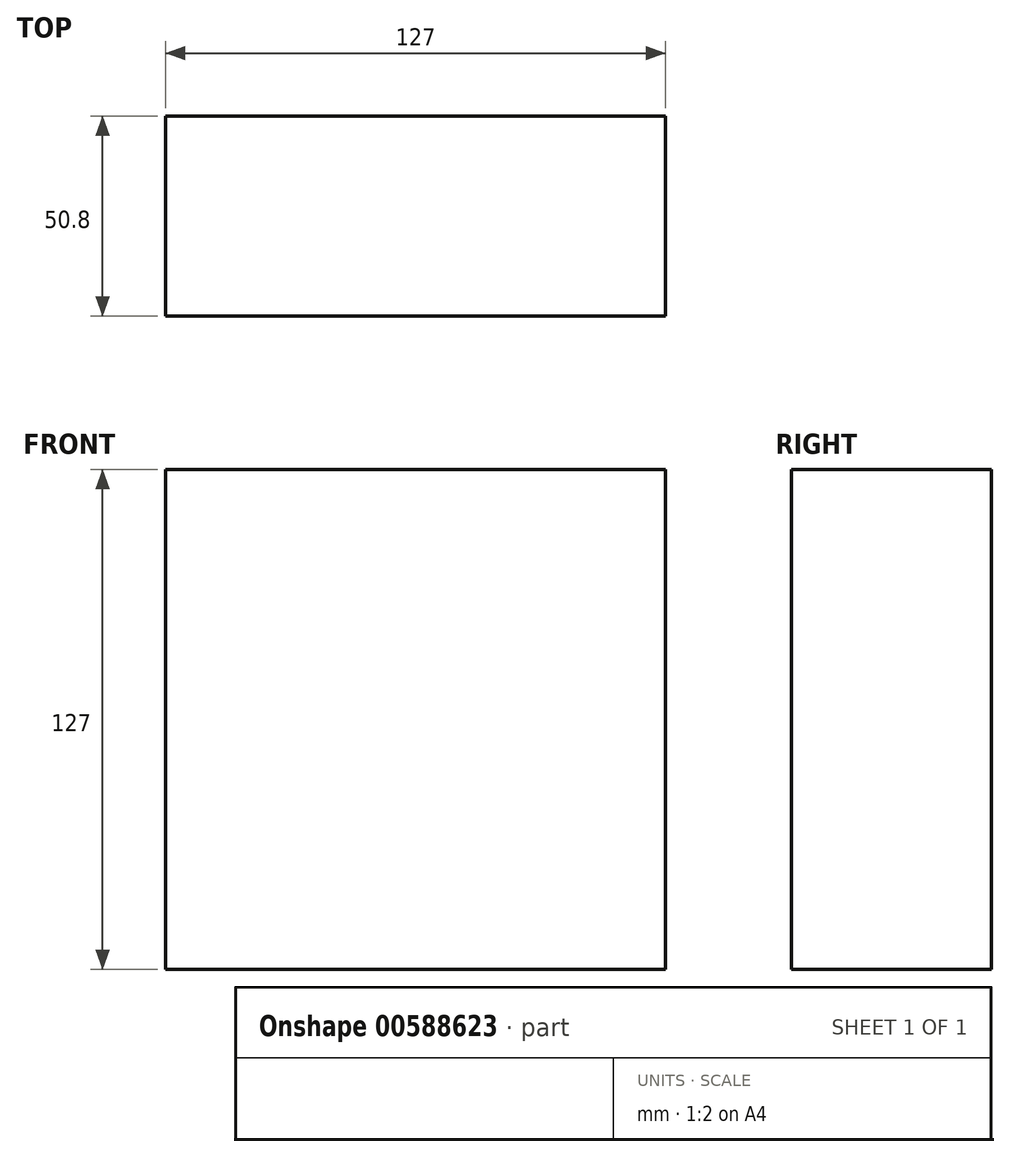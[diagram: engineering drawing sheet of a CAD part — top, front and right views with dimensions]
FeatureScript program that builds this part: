
annotation { "Feature Type Name" : "Feature", "Feature Type Description" : "" }
export const myFeature = defineFeature(function(context is Context, id is Id, definition is map)
    precondition{}
    {
        {
            var Q0;
            Q0=qCreatedBy(makeId("Front.planeOp"),FACE);
            var sketch = newSketch(context, id + "F0", { "sketchPlane" : qUnion([Q0])});
            skLineSegment(sketch, "E0.bottom", {"start": v(63.5, -63.5) * mm, "end": v(-63.5, -63.5) * mm});
            skLineSegment(sketch, "E0.top", {"start": v(63.5, 63.5) * mm, "end": v(-63.5, 63.5) * mm});
            skLineSegment(sketch, "E0.left", {"start": v(63.5, -63.5) * mm, "end": v(63.5, 63.5) * mm});
            skLineSegment(sketch, "E0.right", {"start": v(-63.5, -63.5) * mm, "end": v(-63.5, 63.5) * mm});
            skPoint(sketch, "E0.middle", {"position": v(0, 0) * mm});
            skSolve(sketch);
        }
        {
            var Q0;
            Q0 = qSketchRegion(id + "F0", true);
            extrude(context, id + "F1", {"entities" : qUnion([Q0]), "oppositeDirection" : true, "depth" : 50.8 * mm, "offsetDistance" : 25.4 * mm});
        }
    });
